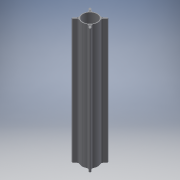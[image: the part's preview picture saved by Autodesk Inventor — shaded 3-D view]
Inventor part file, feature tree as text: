
AUTODESK INVENTOR PART (.ipt)
format: ipt  version: 2016 (Build 200138000, 138)  size: 290,816 bytes
history: native  units: mm
features: extrude x4, sketch x4, projected_geometry x1
ambient origin geometry x8: Origin, YZ Plane, XZ Plane, XY Plane, X Axis, Y Axis, Z Axis, Center Point
bodies: Solid1 (feature_tree)
feature tree (9):
  extrude  "Extrusion1"  Depth=250.0mm TaperAngle=0.0deg
  extrude  "Extrusion2"  Depth=102.676337mm
  extrude  "Extrusion3"  Depth=95.0mm TaperAngle=0.0deg
  extrude  "Extrusion4"  [1 undecoded]
  sketch  "Sketch1"  dims[d0=400.0mm d1=0.0mm d2=250.0mm d3=0.0mm]
  sketch  "Sketch2"  dims[d4=50.0mm d5=102.676337mm]
  sketch  "Sketch3"  dims[d6=3.004552mm d7=95.0mm d8=0.0mm]
  sketch  "Sketch4"  dims[d9=540.0mm d10=0.0mm]
  projected_geometry  "Projected Loop1"
note: 1 required parameter value undecoded (feature->parameter linkage not recoverable at this tier; creation-order binding heuristic only, values carry confidence <= 0.55)
